# Revit family: LCS4238A5T,A2T,A5B,A2B
name_source: partatom
category: Plumbing Fixtures
revit_build: Autodesk Revit LT 2014 (Build: 20130308_1515(x64)
units: mm (PartAtom-declared; Revit-internal decimal feet)

## types (4) — shared parameters
Assembly Code = D2010710
Keynote = 22 40 00.B3
Manufacturer = Best Bath Systems
Type Comments = ADA Compliant
URL = http://www.best-bath.com
Unit Width = 3' - 6 1/4"

## per-type parameters (varying)
| type | Description | Threshold Height | Unit Height |
| LCS4238A5T | Classic Tile, Traditional Bull Nose Threshold | 0' - 0 5/8" | 6' - 6 5/8" |
| LCS4238A5B | Classic Tile, Beveled Threshold | 0' - 0 5/8" | 6' - 6 5/8" |
| LCS4238A2T | Classic Tile, Traditional Bull Nose Threshold | 0' - 2" | 6' - 8" |
| LCS4238A2B | Classic Tile, Beveled Threshold | 0' - 2" | 6' - 8" |

note: column(s) folded — value = type name in every type: Model

## geometry (parser evidence)
native form markers: Blend x25, Sweep x6
no freeform markers — native parametric forms only
